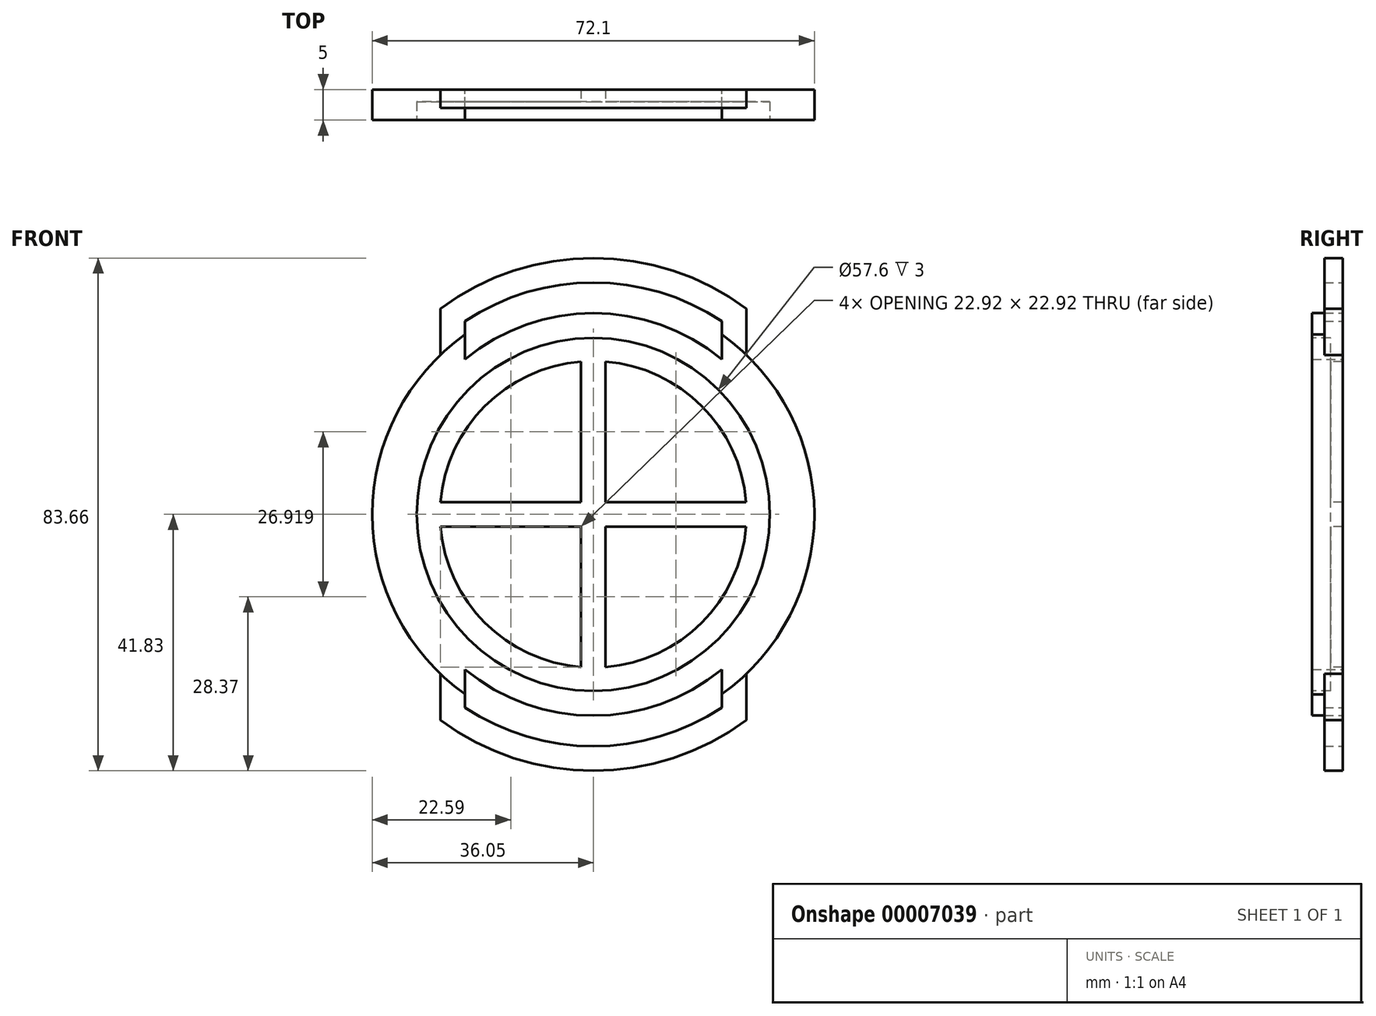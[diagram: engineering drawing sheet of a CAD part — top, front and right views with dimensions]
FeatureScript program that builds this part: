
annotation { "Feature Type Name" : "Feature", "Feature Type Description" : "" }
export const myFeature = defineFeature(function(context is Context, id is Id, definition is map)
    precondition{}
    {
        {
            var Q0;
            Q0=qCreatedBy(makeId("Front.planeOp"),FACE);
            var sketch = newSketch(context, id + "F0", { "sketchPlane" : qUnion([Q0])});
            skCircle(sketch, "E0", {"center": v(0, 0) * mm, "radius": 36.05 * mm});
            skSolve(sketch);
        }
        {
            var Q0;
            Q0 = qSketchRegion(id + "F0", true);
            extrude(context, id + "F1", {"entities" : qUnion([Q0]), "depth" : 5 * mm});
        }
        {
            var Q0;
            Q0=makeQuery(id+"F1.opExtrude","CAP_FACE",FACE,{"disambiguationData":[OSD([sQuery(id+"F0.wireOp",EDGE,"E0")])],"isStart":false});
            var sketch = newSketch(context, id + "F2", { "sketchPlane" : qUnion([Q0])});
            skCircle(sketch, "E1", {"center": v(0, 0) * mm, "radius": 28.8 * mm});
            skSolve(sketch);
        }
        {
            var Q0;
            Q0=makeQuery(id+"F2.imprint","IMPRINT",FACE,{"disambiguationData":[TD([[makeQuery(id+"F2.imprint","IMPRINT",EDGE,{"derivedFrom":sQuery(id+"F2.wireOp",EDGE,"E1")}),1.0]])]});
            var sketch = newSketch(context, id + "F3", { "sketchPlane" : qUnion([Q0])});
            skCircle(sketch, "E2", {"center": v(0, 0) * mm, "radius": 25 * mm});
            skLineSegment(sketch, "E3", {"start": v(-25, 0) * mm, "end": v(25, 0) * mm, "construction": true});
            skLineSegment(sketch, "E4", {"start": v(-24.92, 2) * mm, "end": v(-2, 2) * mm});
            skLineSegment(sketch, "E5", {"start": v(-2, 2) * mm, "end": v(-2, 24.92) * mm});
            skLineSegment(sketch, "E6", {"start": v(2, 24.92) * mm, "end": v(2, 2) * mm});
            skLineSegment(sketch, "E7", {"start": v(2, 2) * mm, "end": v(24.92, 2) * mm});
            skLineSegment(sketch, "E8", {"start": v(24.92, -2) * mm, "end": v(2, -2) * mm});
            skLineSegment(sketch, "E9", {"start": v(2, -2) * mm, "end": v(2, -24.92) * mm});
            skLineSegment(sketch, "E10", {"start": v(-2, -24.92) * mm, "end": v(-2, -2) * mm});
            skLineSegment(sketch, "E11", {"start": v(-2, -2) * mm, "end": v(-24.92, -2) * mm});
            skLineSegment(sketch, "E12", {"start": v(-20.72, 2) * mm, "end": v(-20.72, -2) * mm, "construction": true});
            skPoint(sketch, "E13", {"position": v(-20.72, 0) * mm});
            skLineSegment(sketch, "E14", {"start": v(0, 25) * mm, "end": v(0, -25) * mm, "construction": true});
            skLineSegment(sketch, "E15", {"start": v(-2, 14.15) * mm, "end": v(2, 14.15) * mm});
            skPoint(sketch, "E16", {"position": v(0, 14.15) * mm});
            skSolve(sketch);
        }
        {
            var Q0;
            Q0 = qSketchRegion(id + "F2", true);
            extrude(context, id + "F4", {"entities" : qUnion([Q0]), "operationType" : NewBodyOperationType.REMOVE, "oppositeDirection" : true, "depth" : 3 * mm});
        }
        {
            var Q0;
            {var subQ0=sQuery(id+"F3.wireOp",EDGE,"E7");Q0=makeQuery(id+"F3.imprint","IMPRINT",FACE,{"disambiguationData":[TD([[makeQuery(id+"F3.imprint","IMPRINT",EDGE,{"derivedFrom":subQ0}),1.0]])]});}
            var Q1;
            {var subQ1=sQuery(id+"F3.wireOp",EDGE,"E8");Q1=makeQuery(id+"F3.imprint","IMPRINT",FACE,{"disambiguationData":[TD([[makeQuery(id+"F3.imprint","IMPRINT",EDGE,{"derivedFrom":subQ1}),1.0]])]});}
            var Q2;
            {var subQ1=sQuery(id+"F3.wireOp",EDGE,"E10");Q2=makeQuery(id+"F3.imprint","IMPRINT",FACE,{"disambiguationData":[TD([[makeQuery(id+"F3.imprint","IMPRINT",EDGE,{"derivedFrom":subQ1}),1.0]])]});}
            var Q3;
            {var subQ4=sQuery(id+"F3.wireOp",EDGE,"E4");Q3=makeQuery(id+"F3.imprint","IMPRINT",FACE,{"disambiguationData":[TD([[makeQuery(id+"F3.imprint","IMPRINT",EDGE,{"derivedFrom":subQ4}),1.0]])]});}
            extrude(context, id + "F5", {"entities" : qUnion([Q0, Q1, Q2, Q3]), "operationType" : NewBodyOperationType.REMOVE, "oppositeDirection" : true, "depth" : 6.35 * mm});
        }
        {
            var Q0;
            Q0=makeQuery(id+"F1.opExtrude","CAP_FACE",FACE,{"disambiguationData":[OSD([sQuery(id+"F0.wireOp",EDGE,"E0")])],"isStart":true});
            var sketch = newSketch(context, id + "F6", { "sketchPlane" : qUnion([Q0])});
            skLineSegment(sketch, "E17.rect.bottom", {"start": v(24.94, 41.83) * mm, "end": v(-24.94, 41.83) * mm});
            skLineSegment(sketch, "E17.rect.top", {"start": v(24.94, -41.83) * mm, "end": v(-24.94, -41.83) * mm});
            skLineSegment(sketch, "E17.rect.left", {"start": v(24.94, 41.83) * mm, "end": v(24.94, -41.83) * mm});
            skLineSegment(sketch, "E17.rect.right", {"start": v(-24.94, 41.83) * mm, "end": v(-24.94, -41.83) * mm});
            skPoint(sketch, "E17.rect.middle", {"position": v(0, 0) * mm});
            skCircle(sketch, "E18", {"center": v(0, 0) * mm, "radius": 32.82 * mm, "construction": true});
            skSolve(sketch);
        }
        {
            var Q0;
            {var subQ5=sQuery(id+"F6.wireOp",EDGE,"E17.rect.top");Q0=makeQuery(id+"F6.imprint","IMPRINT",FACE,{"disambiguationData":[TD([[makeQuery(id+"F6.imprint","IMPRINT",EDGE,{"derivedFrom":subQ5}),-1.0]])]});}
            var Q1;
            {var subQ5=sQuery(id+"F6.wireOp",EDGE,"E17.rect.bottom");Q1=makeQuery(id+"F6.imprint","IMPRINT",FACE,{"disambiguationData":[TD([[makeQuery(id+"F6.imprint","IMPRINT",EDGE,{"derivedFrom":subQ5}),1.0]])]});}
            extrude(context, id + "F7", {"entities" : qUnion([Q0, Q1]), "operationType" : NewBodyOperationType.ADD, "oppositeDirection" : true, "depth" : 3 * mm});
        }
        {
            var Q0;
            {var subQ0=sQuery(id+"F0.wireOp",EDGE,"E0");var subQ1=sQuery(id+"F6.wireOp",EDGE,"E17.rect.left");var subQ2=sQuery(id+"F6.wireOp",EDGE,"E17.rect.right");Q0=makeQuery(id+"F7.boolean.opBoolean","MERGE",FACE,{"derivedFrom":[makeQuery(id+"F1.opExtrude","CAP_FACE",FACE,{"disambiguationData":[OSD([subQ0])],"isStart":true}),makeQuery(id+"F7.opExtrude","CAP_FACE",FACE,{"disambiguationData":[OSD([subQ0,sQuery(id+"F6.wireOp",EDGE,"E17.rect.bottom"),subQ1,subQ2])],"isStart":true}),makeQuery(id+"F7.opExtrude","CAP_FACE",FACE,{"disambiguationData":[OSD([subQ0,sQuery(id+"F6.wireOp",EDGE,"E17.rect.top"),subQ1,subQ2])],"isStart":true})]});}
            var sketch = newSketch(context, id + "F8", { "sketchPlane" : qUnion([Q0])});
            skCircle(sketch, "E19", {"center": v(0, 0) * mm, "radius": 32.83 * mm});
            skLineSegment(sketch, "E20", {"start": v(0, 37.83) * mm, "end": v(0, 32.83) * mm, "construction": true});
            skArc(sketch, "E21", {"start": v(-20.94, -30.29) * mm, "mid": v(0, -37.83) * mm, "end": v(20.94, -30.29) * mm});
            skLineSegment(sketch, "E22", {"start": v(0, -37.83) * mm, "end": v(0, -41.83) * mm});
            skLineSegment(sketch, "E23", {"start": v(20.94, -30.29) * mm, "end": v(20.94, -25.29) * mm});
            skLineSegment(sketch, "E24", {"start": v(-20.94, -30.29) * mm, "end": v(-20.94, -25.29) * mm});
            skLineSegment(sketch, "E25", {"start": v(0, -37.83) * mm, "end": v(0, -32.83) * mm, "construction": true});
            skLineSegment(sketch, "E26", {"start": v(20.94, 25.29) * mm, "end": v(20.94, 30.29) * mm});
            skLineSegment(sketch, "E27", {"start": v(-20.94, 25.29) * mm, "end": v(-20.94, 30.29) * mm});
            skArc(sketch, "E28", {"start": v(20.94, 30.29) * mm, "mid": v(0, 37.83) * mm, "end": v(-20.94, 30.29) * mm});
            skSolve(sketch);
        }
        {
            var Q0;
            {var subQ1=sQuery(id+"F8.wireOp",EDGE,"E26");Q0=makeQuery(id+"F8.imprint","IMPRINT",FACE,{"disambiguationData":[TD([[makeQuery(id+"F8.imprint","IMPRINT",EDGE,{"derivedFrom":subQ1}),1.0]])]});}
            var Q1;
            {var subQ1=sQuery(id+"F8.wireOp",EDGE,"E24");Q1=makeQuery(id+"F8.imprint","IMPRINT",FACE,{"disambiguationData":[TD([[makeQuery(id+"F8.imprint","IMPRINT",EDGE,{"derivedFrom":subQ1}),-1.0]])]});}
            extrude(context, id + "F9", {"entities" : qUnion([Q0, Q1]), "operationType" : NewBodyOperationType.REMOVE, "oppositeDirection" : true, "depth" : 25.4 * mm});
        }
        {
            var Q0;
            {var subQ0=sQuery(id+"F0.wireOp",EDGE,"E0");var subQ1=sQuery(id+"F6.wireOp",EDGE,"E17.rect.left");var subQ2=sQuery(id+"F6.wireOp",EDGE,"E17.rect.right");Q0=makeQuery(id+"F7.boolean.opBoolean","MERGE",FACE,{"derivedFrom":[makeQuery(id+"F1.opExtrude","CAP_FACE",FACE,{"disambiguationData":[OSD([subQ0])],"isStart":true}),makeQuery(id+"F7.opExtrude","CAP_FACE",FACE,{"disambiguationData":[OSD([subQ0,sQuery(id+"F6.wireOp",EDGE,"E17.rect.bottom"),subQ1,subQ2])],"isStart":true}),makeQuery(id+"F7.opExtrude","CAP_FACE",FACE,{"disambiguationData":[OSD([subQ0,sQuery(id+"F6.wireOp",EDGE,"E17.rect.top"),subQ1,subQ2])],"isStart":true})]});}
            var sketch = newSketch(context, id + "F10", { "sketchPlane" : qUnion([Q0])});
            skCircle(sketch, "E29", {"center": v(0, 0) * mm, "radius": 37.83 * mm});
            skCircle(sketch, "E30", {"center": v(0, 0) * mm, "radius": 41.83 * mm});
            skCircle(sketch, "E31", {"center": v(0, 0) * mm, "radius": 32.83 * mm});
            skLineSegment(sketch, "E32", {"start": v(20.94, 25.29) * mm, "end": v(20.94, 31.5) * mm});
            skLineSegment(sketch, "E33", {"start": v(-20.94, 25.29) * mm, "end": v(-20.94, 31.5) * mm});
            skLineSegment(sketch, "E34", {"start": v(-20.94, -25.29) * mm, "end": v(-20.94, -31.5) * mm});
            skLineSegment(sketch, "E35", {"start": v(20.94, -25.29) * mm, "end": v(20.94, -31.5) * mm});
            skLineSegment(sketch, "E36", {"start": v(24.94, 33.58) * mm, "end": v(24.94, 41.83) * mm});
            skLineSegment(sketch, "E37", {"start": v(24.94, 41.83) * mm, "end": v(-24.94, 41.83) * mm});
            skLineSegment(sketch, "E38", {"start": v(-24.94, 41.83) * mm, "end": v(-24.94, 33.58) * mm});
            skLineSegment(sketch, "E39", {"start": v(-24.94, -33.58) * mm, "end": v(-24.94, -41.83) * mm});
            skLineSegment(sketch, "E40", {"start": v(-24.94, -41.83) * mm, "end": v(24.94, -41.83) * mm});
            skLineSegment(sketch, "E41", {"start": v(24.94, -41.83) * mm, "end": v(24.94, -33.58) * mm});
            skSolve(sketch);
        }
        {
            var Q0;
            {var subQ3=sQuery(id+"F10.wireOp",EDGE,"E39");Q0=makeQuery(id+"F10.imprint","IMPRINT",FACE,{"disambiguationData":[TD([[makeQuery(id+"F10.imprint","IMPRINT",EDGE,{"derivedFrom":subQ3}),1.0]])]});}
            var Q1;
            {var subQ3=sQuery(id+"F10.wireOp",EDGE,"E41");Q1=makeQuery(id+"F10.imprint","IMPRINT",FACE,{"disambiguationData":[TD([[makeQuery(id+"F10.imprint","IMPRINT",EDGE,{"derivedFrom":subQ3}),-1.0]])]});}
            var Q2;
            {var subQ1=sQuery(id+"F10.wireOp",EDGE,"E29");var subQ3=sQuery(id+"F10.wireOp",EDGE,"E35");var subQ5=makeQuery(id+"F10.imprint","INTERSECT",VERTEX,{"derivedFrom":[subQ1,subQ3]});Q2=makeQuery(id+"F10.imprint","IMPRINT",FACE,{"disambiguationData":[TD([[makeQuery(id+"F10.imprint","IMPRINT",EDGE,{"disambiguationData":[TD([[subQ5,1.0]])],"derivedFrom":subQ1}),1.0]])]});}
            var Q3;
            {var subQ1=sQuery(id+"F10.wireOp",EDGE,"E29");var subQ3=sQuery(id+"F10.wireOp",EDGE,"E34");var subQ5=makeQuery(id+"F10.imprint","INTERSECT",VERTEX,{"derivedFrom":[subQ1,subQ3]});Q3=makeQuery(id+"F10.imprint","IMPRINT",FACE,{"disambiguationData":[TD([[makeQuery(id+"F10.imprint","IMPRINT",EDGE,{"disambiguationData":[TD([[subQ5,-1.0]])],"derivedFrom":subQ1}),1.0]])]});}
            var Q4;
            {var subQ0=sQuery(id+"F10.wireOp",EDGE,"E38");Q4=makeQuery(id+"F10.imprint","IMPRINT",FACE,{"disambiguationData":[TD([[makeQuery(id+"F10.imprint","IMPRINT",EDGE,{"derivedFrom":subQ0}),1.0]])]});}
            var Q5;
            {var subQ1=sQuery(id+"F10.wireOp",EDGE,"E29");var subQ3=sQuery(id+"F10.wireOp",EDGE,"E33");var subQ5=makeQuery(id+"F10.imprint","INTERSECT",VERTEX,{"derivedFrom":[subQ1,subQ3]});Q5=makeQuery(id+"F10.imprint","IMPRINT",FACE,{"disambiguationData":[TD([[makeQuery(id+"F10.imprint","IMPRINT",EDGE,{"disambiguationData":[TD([[subQ5,1.0]])],"derivedFrom":subQ1}),1.0]])]});}
            var Q6;
            {var subQ3=sQuery(id+"F10.wireOp",EDGE,"E36");Q6=makeQuery(id+"F10.imprint","IMPRINT",FACE,{"disambiguationData":[TD([[makeQuery(id+"F10.imprint","IMPRINT",EDGE,{"derivedFrom":subQ3}),-1.0]])]});}
            var Q7;
            {var subQ1=sQuery(id+"F10.wireOp",EDGE,"E29");var subQ3=sQuery(id+"F10.wireOp",EDGE,"E32");var subQ5=makeQuery(id+"F10.imprint","INTERSECT",VERTEX,{"derivedFrom":[subQ1,subQ3]});Q7=makeQuery(id+"F10.imprint","IMPRINT",FACE,{"disambiguationData":[TD([[makeQuery(id+"F10.imprint","IMPRINT",EDGE,{"disambiguationData":[TD([[subQ5,-1.0]])],"derivedFrom":subQ1}),1.0]])]});}
            extrude(context, id + "F11", {"entities" : qUnion([Q0, Q1, Q2, Q3, Q4, Q5, Q6, Q7]), "operationType" : NewBodyOperationType.REMOVE, "oppositeDirection" : true, "depth" : 25.4 * mm});
        }
    });
